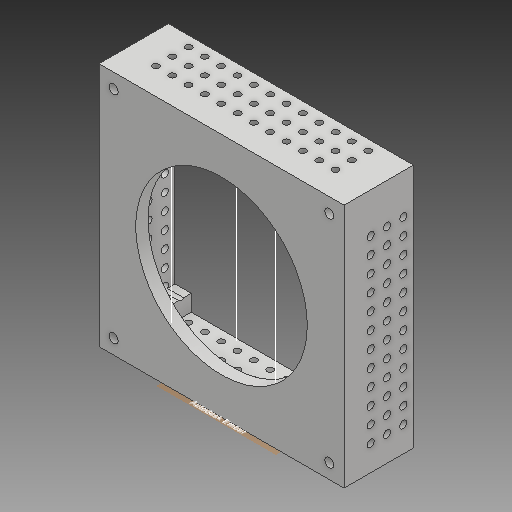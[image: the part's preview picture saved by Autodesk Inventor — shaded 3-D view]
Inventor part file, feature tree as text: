
AUTODESK INVENTOR PART (.ipt)
format: ipt  version: 2018 (Build 220112000, 112)  size: 537,600 bytes
history: native  units: mm
features: sketch x13, extrude x8, pattern_linear x3
ambient origin geometry x8: Origin, YZ Plane, XZ Plane, XY Plane, X Axis, Y Axis, Z Axis, Center Point
bodies: Solid1 (feature_tree)
feature tree (24):
  sketch  "Sketch1"  dims[d0=150.0mm d1=150.0mm]
  extrude  "Extrusion1"  Depth=150.0mm
  extrude  "Extrusion3"  Depth=4.0mm
  extrude  "Extrusion4"  Depth=10.0mm
  pattern_linear  "Rectangular Pattern1"  Count1=2 Spacing1=132.0mm
  extrude  "Extrusion5"  Depth=80.0mm
  pattern_linear  "Rectangular Pattern2"  Count1=8 Spacing1=0.0mm
  sketch  "Sketch9"  dims[d17=20.0mm d19=132.0mm d20=5.5mm d21=80.0mm d22=0.0mm]
  extrude  "Extrusion8"  Depth=132.0mm
  sketch  "Sketch11"  dims[d45=70.0mm d46=0.0mm d47=6.5mm d48=70.0mm d49=0.0mm]
  extrude  "Extrusion9"  Depth=6.5mm
  pattern_linear  "Rectangular Pattern5"  Count1=7 Spacing1=0.0mm
  extrude  "Extrusion10"  Depth=80.0mm
  sketch  "Sketch14"  dims[d57=12.5mm]
  sketch  "Sketch15"  dims[d58=70.0mm d59=0.0mm]
  extrude  "Extrusion11"  Depth=7.5mm TaperAngle=0.0deg
  sketch  "Sketch2"  dims[d2=7.5mm d3=0.0mm d7=4.0mm]
  sketch  "Sketch4"  dims[d8=35.0mm d9=0.0mm d10=10.0mm]
  sketch  "Sketch5"  dims[d11=10.0mm]
  sketch  "Sketch6"  dims[d12=35.0mm d13=0.0mm d14=20.0mm d16=132.0mm]
  sketch  "Sketch10"  dims[d23=20.0mm d25=132.0mm d26=20.0mm d28=132.0mm]
  sketch  "Sketch12"  dims[d50=30.0mm d52=10.0mm d53=80.0mm]
  sketch  "Sketch13"  dims[d54=7.5mm d55=70.0mm d56=0.0mm]
  sketch  "Sketch16"
